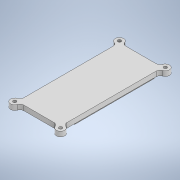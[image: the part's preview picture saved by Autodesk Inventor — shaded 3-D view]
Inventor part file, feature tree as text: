
AUTODESK INVENTOR PART (.ipt)
format: ipt  version: 2020 (Build 240168000, 168)  size: 167,424 bytes
history: native  units: in
note: dims shown in document units (in); Inventor stores cm internally (conversion verified against a paired STEP export)
features: extrude x3, fillet x3, mirror x3, sketch x3, plane x2, projected_geometry x2
ambient origin geometry x8: Origin, YZ Plane, XZ Plane, XY Plane, X Axis, Y Axis, Z Axis, Center Point
bodies: Solid1 (feature_tree)
feature tree (16):
  extrude  "Extrusion1"  Depth=1.33in
  extrude  "Extrusion2"  Depth=1.05in
  extrude  "Extrusion3"  Depth=0.13in
  fillet  "Fillet1"  Radius=0.13in
  plane  "Work Plane1"
  plane  "Work Plane2"
  mirror  "Mirror1"
  mirror  "Mirror2"
  mirror  "Mirror3"
  fillet  "Fillet2"  Radius=0.15in
  fillet  "Fillet3"  Radius=0.1in
  sketch  "Sketch1"  dims[d0=3.15in d1=1.33in]
  sketch  "Sketch2"  dims[d2=0.15in d3=0.0in d4=1.05in]
  projected_geometry  "Projected Loop1"
  sketch  "Sketch3"  dims[d5=2.45in d6=0.13in d7=0.13in d8=0.15in d9=0.0in d10=0.1in d11=0.08in d12=0.08in d13=0.13in d14=0.15in d15=0.0in d16=0.125in d17=0.125in d18=0.125in]
  projected_geometry  "Projected Loop2"
